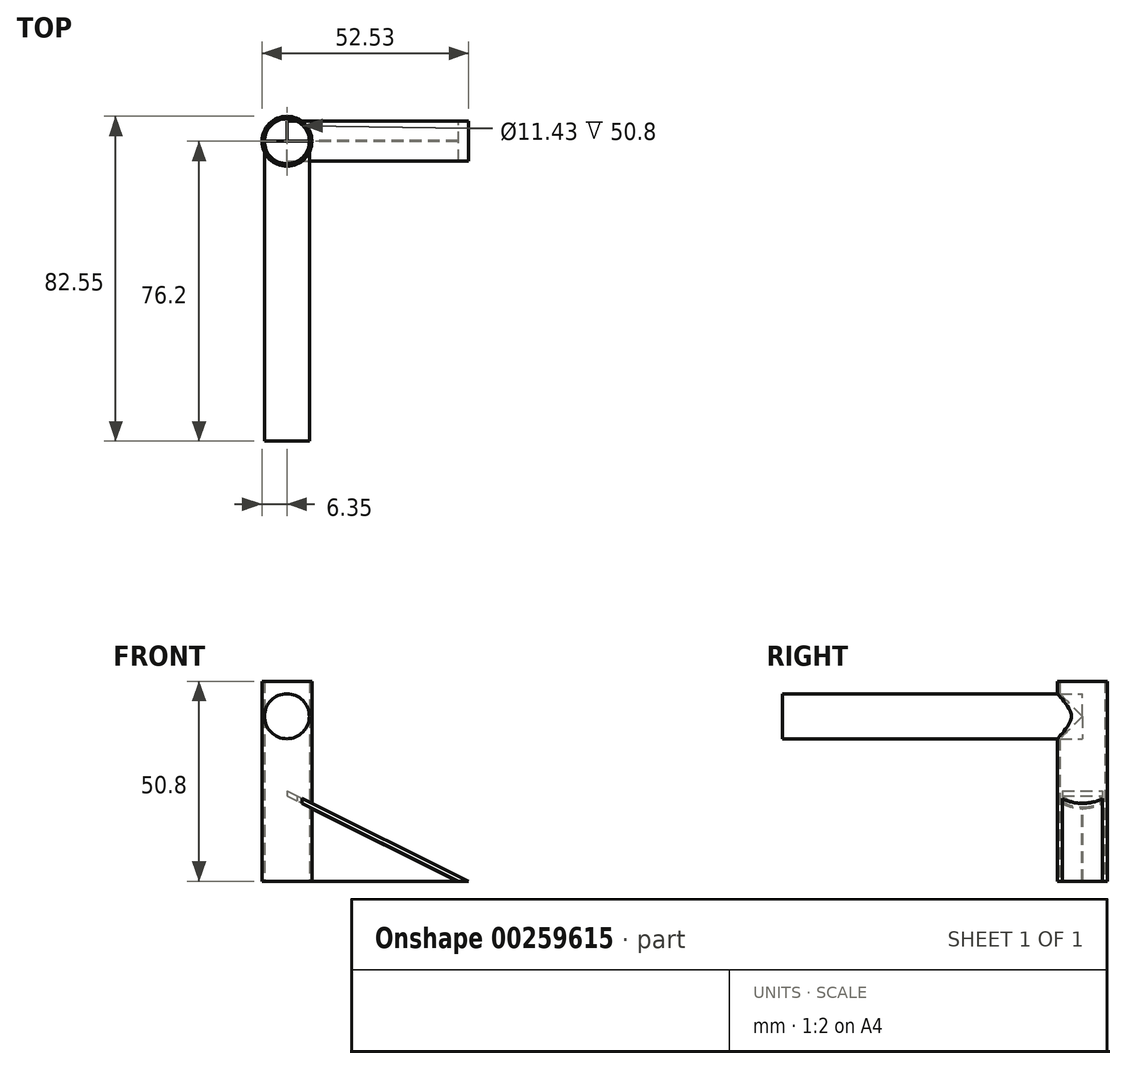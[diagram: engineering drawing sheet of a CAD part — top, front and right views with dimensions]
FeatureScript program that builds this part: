
annotation { "Feature Type Name" : "Feature", "Feature Type Description" : "" }
export const myFeature = defineFeature(function(context is Context, id is Id, definition is map)
    precondition{}
    {
        {
            var Q0;
            Q0=qCreatedBy(makeId("Top.planeOp"),FACE);
            var sketch = newSketch(context, id + "F0", { "sketchPlane" : qUnion([Q0])});
            skCircle(sketch, "E0", {"center": v(0, 0) * mm, "radius": 5.72 * mm});
            skCircle(sketch, "E1", {"center": v(0, 0) * mm, "radius": 6.35 * mm});
            skSolve(sketch);
        }
        {
            var Q0;
            Q0=makeQuery(id+"F0.imprint","IMPRINT",FACE,{"disambiguationData":[TD([[makeQuery(id+"F0.imprint","IMPRINT",EDGE,{"derivedFrom":sQuery(id+"F0.wireOp",EDGE,"E0")}),-1.0]])]});
            extrude(context, id + "F1", {"entities" : qUnion([Q0]), "depth" : 50.8 * mm});
        }
        {
            var Q0;
            Q0=qCreatedBy(makeId("Front.planeOp"),FACE);
            var sketch = newSketch(context, id + "F2", { "sketchPlane" : qUnion([Q0])});
            skCircle(sketch, "E2", {"center": v(0, 41.91) * mm, "radius": 5.72 * mm});
            skSolve(sketch);
        }
        {
            var Q0;
            Q0 = qSketchRegion(id + "F2", true);
            extrude(context, id + "F3", {"entities" : qUnion([Q0]), "operationType" : NewBodyOperationType.ADD, "depth" : 76.2 * mm});
        }
        {
            var Q0;
            Q0=qCreatedBy(makeId("Front.planeOp"),FACE);
            var sketch = newSketch(context, id + "F4", { "sketchPlane" : qUnion([Q0])});
            skLineSegment(sketch, "E3", {"start": v(0, 22.94) * mm, "end": v(46.18, 0) * mm});
            skLineSegment(sketch, "E4", {"start": v(0, 22.94) * mm, "end": v(0, 21.67) * mm});
            skLineSegment(sketch, "E5", {"start": v(0, 21.67) * mm, "end": v(43.63, 0) * mm});
            skLineSegment(sketch, "E6", {"start": v(43.63, 0) * mm, "end": v(46.18, 0) * mm});
            skSolve(sketch);
        }
        {
            var Q0;
            Q0=makeQuery(id+"F4.imprint","IMPRINT",FACE,{"disambiguationData":[TD([[makeQuery(id+"F4.imprint","IMPRINT",EDGE,{"derivedFrom":sQuery(id+"F4.wireOp",EDGE,"E3")}),-1.0]])]});
            extrude(context, id + "F5", {"entities" : qUnion([Q0]), "operationType" : NewBodyOperationType.ADD, "depth" : 10.16 * mm, "symmetric" : true});
        }
        {
            var Q0;
            Q0=qCreatedBy(makeId("Front.planeOp"),FACE);
            var sketch = newSketch(context, id + "F6", { "sketchPlane" : qUnion([Q0])});
            skLineSegment(sketch, "E7", {"start": v(6.45, 18.36) * mm, "end": v(6.45, 0) * mm});
            skLineSegment(sketch, "E8", {"start": v(6.45, 0) * mm, "end": v(43.38, 0) * mm});
            skLineSegment(sketch, "E9", {"start": v(43.38, 0) * mm, "end": v(6.45, 18.36) * mm});
            skSolve(sketch);
        }
        {
            var Q0;
            Q0 = qSketchRegion(id + "F6", true);
            extrude(context, id + "F7", {"entities" : qUnion([Q0]), "depth" : 0.25 * mm, "symmetric" : true});
        }
    });
